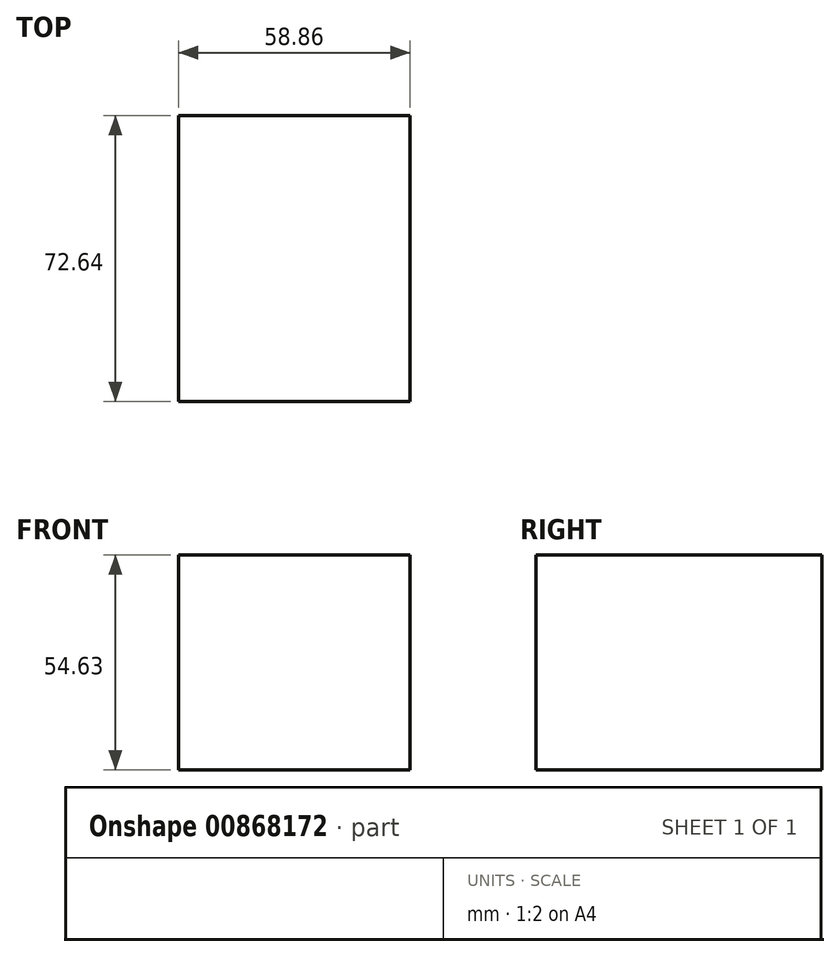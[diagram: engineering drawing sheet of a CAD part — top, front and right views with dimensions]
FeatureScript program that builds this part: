
annotation { "Feature Type Name" : "Feature", "Feature Type Description" : "" }
export const myFeature = defineFeature(function(context is Context, id is Id, definition is map)
    precondition{}
    {
        {
            var Q0;
            Q0=qCreatedBy(makeId("Front.planeOp"),FACE);
            var sketch = newSketch(context, id + "F0", { "sketchPlane" : qUnion([Q0])});
            skLineSegment(sketch, "E0.bottom", {"start": v(-58.86, 54.63) * mm, "end": v(0, 54.63) * mm});
            skLineSegment(sketch, "E0.top", {"start": v(-58.86, 0) * mm, "end": v(0, 0) * mm});
            skLineSegment(sketch, "E0.left", {"start": v(-58.86, 54.63) * mm, "end": v(-58.86, 0) * mm});
            skLineSegment(sketch, "E0.right", {"start": v(0, 54.63) * mm, "end": v(0, 0) * mm});
            skSolve(sketch);
        }
        {
            var Q0;
            Q0 = qSketchRegion(id + "F0", true);
            extrude(context, id + "F1", {"entities" : qUnion([Q0]), "depth" : 72.64 * mm, "offsetDistance" : 25.4 * mm});
        }
    });
